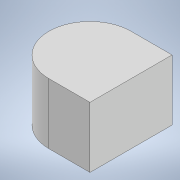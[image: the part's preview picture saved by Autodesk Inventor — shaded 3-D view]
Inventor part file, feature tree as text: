
AUTODESK INVENTOR PART (.ipt)
format: ipt  version: 2022.2 (Build 262287000, 287)  size: 93,184 bytes
history: native  units: mm
features: other x1, extrude x1, sketch x1
ambient origin geometry x8: Origin, YZ Plane, XZ Plane, XY Plane, X Axis, Y Axis, Z Axis, Center Point
bodies: Solid1 (feature_tree)
feature tree (3):
  other  "Crank.ipt"
  extrude  "Extrusion1"  Depth=2.5mm
  sketch  "Sketch1"  dims[d0=10.0mm d1=2.5mm d2=2.5mm d3=5.0mm d4=3.7mm d5=0.0mm]
